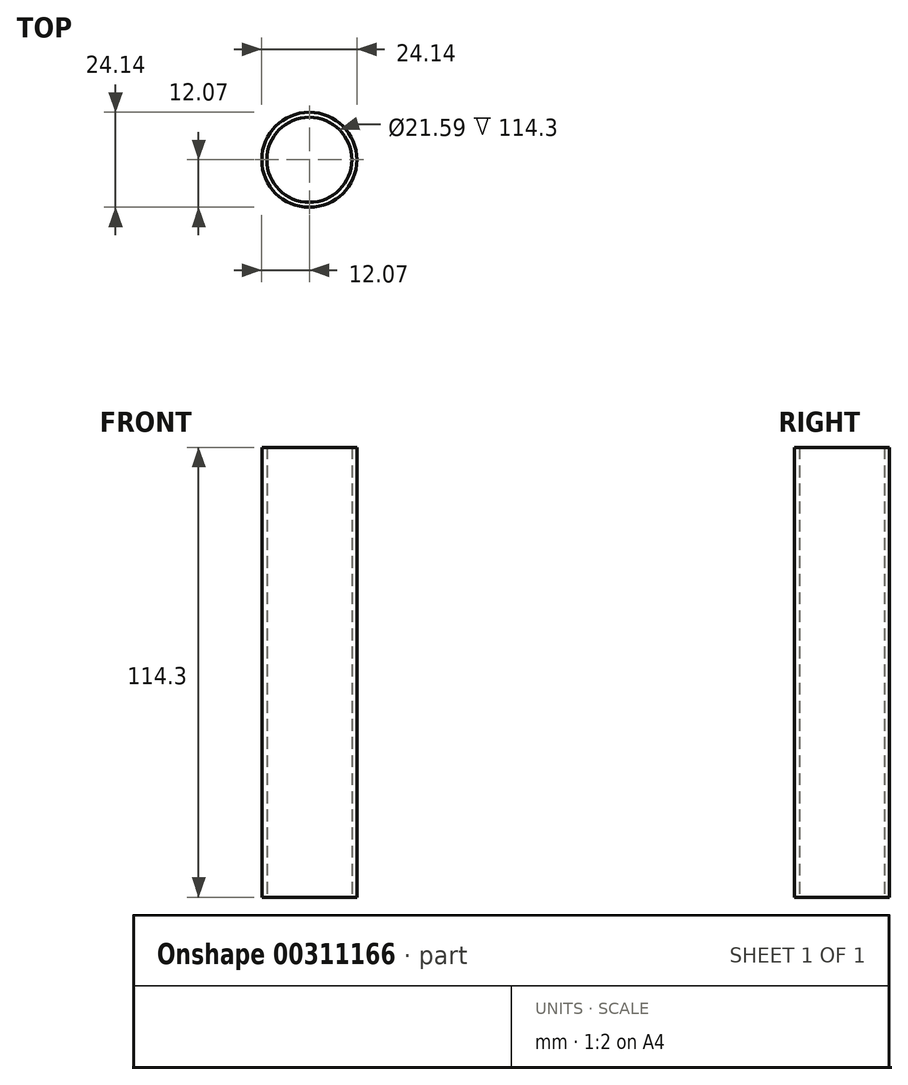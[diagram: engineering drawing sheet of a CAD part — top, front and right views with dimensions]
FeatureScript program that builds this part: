
annotation { "Feature Type Name" : "Feature", "Feature Type Description" : "" }
export const myFeature = defineFeature(function(context is Context, id is Id, definition is map)
    precondition{}
    {
        {
            var Q0;
            Q0=qCreatedBy(makeId("Top.planeOp"),FACE);
            var sketch = newSketch(context, id + "F0", { "sketchPlane" : qUnion([Q0])});
            skCircle(sketch, "E0", {"center": v(0, 0) * mm, "radius": 12.06 * mm});
            skCircle(sketch, "E1", {"center": v(0, 0) * mm, "radius": 10.8 * mm});
            skSolve(sketch);
        }
        {
            var Q0;
            Q0=makeQuery(id+"F0.imprint","IMPRINT",FACE,{"disambiguationData":[TD([[makeQuery(id+"F0.imprint","IMPRINT",EDGE,{"derivedFrom":sQuery(id+"F0.wireOp",EDGE,"E0")}),1.0]])]});
            extrude(context, id + "F1", {"entities" : qUnion([Q0]), "depth" : 114.3 * mm});
        }
    });
